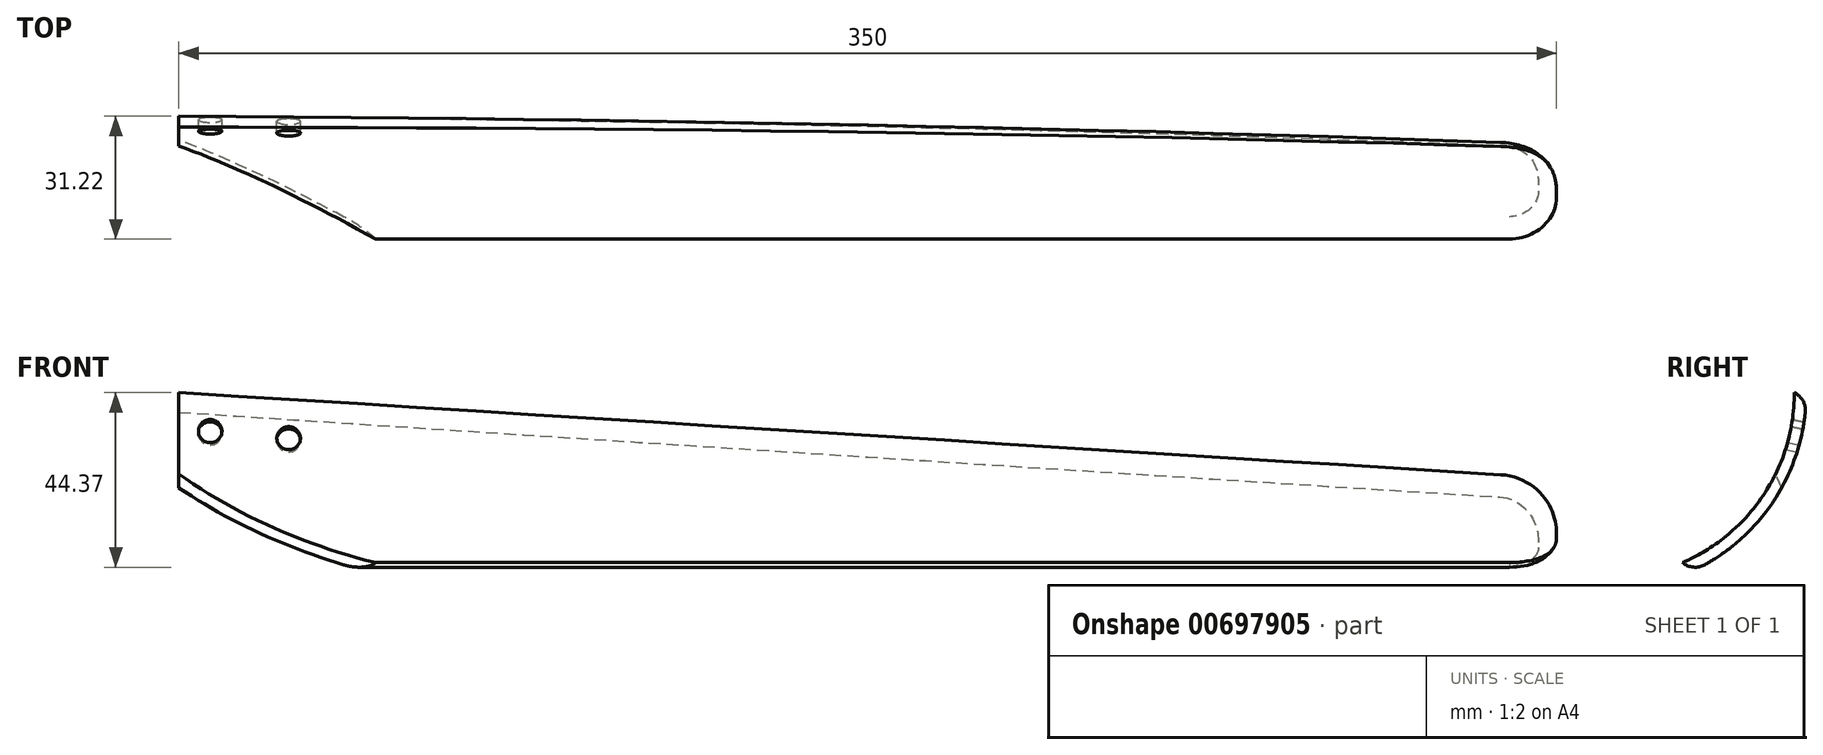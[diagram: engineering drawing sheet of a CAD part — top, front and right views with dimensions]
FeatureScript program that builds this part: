
annotation { "Feature Type Name" : "Feature", "Feature Type Description" : "" }
export const myFeature = defineFeature(function(context is Context, id is Id, definition is map)
    precondition{}
    {
        {
            assignVariable(context, id + "F0", {"name" : "longueur", "anyValue" : 350});
        }
        {
            var Q0;
            Q0=qCreatedBy(makeId("Right.planeOp"),FACE);
            var sketch = newSketch(context, id + "F1", { "sketchPlane" : qUnion([Q0])});
            skCircle(sketch, "E0", {"center": v(0, 0) * mm, "radius": 50 * mm});
            skCircle(sketch, "E1.0", {"center": v(0, 0) * mm, "radius": 47 * mm});
            skLineSegment(sketch, "E2", {"start": v(50, 0) * mm, "end": v(19.75, -45.93) * mm, "construction": true});
            skLineSegment(sketch, "E3", {"start": v(50, 0) * mm, "end": v(47, 0) * mm});
            skLineSegment(sketch, "E4", {"start": v(19.75, -45.93) * mm, "end": v(18.57, -43.18) * mm});
            skLineSegment(sketch, "E5", {"start": v(50, 0) * mm, "end": v(43.75, -24.2) * mm, "construction": true});
            skLineSegment(sketch, "E6", {"start": v(0, 0) * mm, "end": v(50, 0) * mm, "construction": true});
            skLineSegment(sketch, "E7.1.0", {"start": v(0, 0) * mm, "end": v(49.06, -9.65) * mm, "construction": true});
            skLineSegment(sketch, "E7.2.0", {"start": v(0, 0) * mm, "end": v(46.28, -18.93) * mm, "construction": true});
            skLineSegment(sketch, "E7.anchor2", {"start": v(0, 0) * mm, "end": v(19.75, -45.93) * mm, "construction": true});
            skLineSegment(sketch, "E8.2.3.0", {"start": v(0, 0) * mm, "end": v(41.76, -27.5) * mm, "construction": true});
            skLineSegment(sketch, "E8.2.4.0", {"start": v(0, 0) * mm, "end": v(35.67, -35.04) * mm, "construction": true});
            skLineSegment(sketch, "E9.2.5.0", {"start": v(0, 0) * mm, "end": v(28.24, -41.26) * mm, "construction": true});
            skSolve(sketch);
        }
        {
            var Q0;
            {var subQ0=sQuery(id+"F1.wireOp",EDGE,"E3");Q0=makeQuery(id+"F1.imprint","IMPRINT",FACE,{"disambiguationData":[TD([[makeQuery(id+"F1.imprint","IMPRINT",EDGE,{"derivedFrom":subQ0}),1.0]])]});}
            extrude(context, id + "F2", {"entities" : qUnion([Q0]), "depth" : (getVariable(context, 'longueur')) * mm, "offsetDistance" : 25 * mm});
        }
        {
            var Q0;
            Q0=makeQuery(id+"F2.opExtrude","CAP_FACE",FACE,{"disambiguationData":[OSD([sQuery(id+"F1.wireOp",EDGE,"E0"),sQuery(id+"F1.wireOp",EDGE,"E1.0"),sQuery(id+"F1.wireOp",EDGE,"E3"),sQuery(id+"F1.wireOp",EDGE,"E4")])],"isStart":false});
            var sketch = newSketch(context, id + "F3", { "sketchPlane" : qUnion([Q0])});
            skLineSegment(sketch, "E10", {"start": v(19.75, -45.93) * mm, "end": v(45.03, -21.73) * mm});
            skSolve(sketch);
        }
        {
            var Q0;
            Q0=makeQuery(id+"F2.opExtrude","CAP_VERTEX",VERTEX,{"disambiguationData":[OSD([sQuery(id+"F1.wireOp",EDGE,"E1.0"),sQuery(id+"F1.wireOp",EDGE,"E3")])],"isStart":true});
            var Q1;
            Q1=makeQuery(id+"F2.opExtrude","CAP_VERTEX",VERTEX,{"disambiguationData":[OSD([sQuery(id+"F1.wireOp",EDGE,"E0"),sQuery(id+"F1.wireOp",EDGE,"E3")])],"isStart":true});
            var Q2;
            Q2=sQuery(id+"F3.wireOp",VERTEX,"E10.end");
            cPlane(context, id + "F4", {"entities" : qUnion([Q0, Q1, Q2]), "cplaneType" : CPlaneType.THREE_POINT, "offset" : 25 * mm, "width" : 150 * mm, "height" : 150 * mm});
        }
        {
            var Q0;
            Q0=qCreatedBy(id+"F4.planeOp",FACE);
            var sketch = newSketch(context, id + "F5", { "sketchPlane" : qUnion([Q0])});
            skLineSegment(sketch, "E11.0", {"start": v(0, 50) * mm, "end": v(0, 47) * mm});
            skLineSegment(sketch, "E12", {"start": v(0, 50) * mm, "end": v(356.03, 68.4) * mm});
            skLineSegment(sketch, "E13", {"start": v(356.03, 68.4) * mm, "end": v(352, 18.56) * mm});
            skLineSegment(sketch, "E14", {"start": v(352, 18.57) * mm, "end": v(0, 47) * mm});
            skSolve(sketch);
        }
        {
            var Q0;
            Q0=qSketchRegion(id+"F5",true);
            extrude(context, id + "F6", {"entities" : qUnion([Q0]), "operationType" : NewBodyOperationType.REMOVE, "endBound" : BoundingType.THROUGH_ALL, "depth" : 25 * mm, "offsetDistance" : 25 * mm});
        }
        {
            var Q0;
            Q0=makeQuery(id+"F2.opExtrude","SWEPT_FACE",FACE,{"disambiguationData":[OSD([sQuery(id+"F1.wireOp",EDGE,"E4")])]});
            var sketch = newSketch(context, id + "F7", { "sketchPlane" : qUnion([Q0])});
            skLineSegment(sketch, "E15", {"start": v(0, -50) * mm, "end": v(50, -50) * mm});
            skLineSegment(sketch, "E16", {"start": v(50, -50) * mm, "end": v(50, -47) * mm});
            skSolve(sketch);
        }
        {
            var Q0;
            Q0=sQuery(id+"F7.wireOp",VERTEX,"E15.end");
            var Q1;
            Q1=sQuery(id+"F7.wireOp",VERTEX,"E16.end");
            var Q2;
            Q2=sQuery(id+"F1.wireOp",VERTEX,"E5.end");
            cPlane(context, id + "F8", {"entities" : qUnion([Q0, Q1, Q2]), "cplaneType" : CPlaneType.THREE_POINT, "offset" : 25 * mm, "width" : 150 * mm, "height" : 150 * mm});
        }
        {
            var Q0;
            Q0=qCreatedBy(id+"F8.planeOp",FACE);
            var sketch = newSketch(context, id + "F9", { "sketchPlane" : qUnion([Q0])});
            skLineSegment(sketch, "E17.bottom", {"start": v(26.95, -18.07) * mm, "end": v(-72.05, -18.07) * mm});
            skLineSegment(sketch, "E17.top", {"start": v(26.95, -70.26) * mm, "end": v(-72.05, -70.26) * mm});
            skLineSegment(sketch, "E17.left", {"start": v(26.95, -18.07) * mm, "end": v(26.95, -70.26) * mm});
            skLineSegment(sketch, "E17.right", {"start": v(-72.05, -18.07) * mm, "end": v(-72.05, -70.26) * mm});
            skSolve(sketch);
        }
        {
            var Q0;
            Q0=qSketchRegion(id+"F9",true);
            extrude(context, id + "F10", {"entities" : qUnion([Q0]), "operationType" : NewBodyOperationType.REMOVE, "endBound" : BoundingType.THROUGH_ALL, "oppositeDirection" : true, "depth" : 25 * mm, "offsetDistance" : 25 * mm});
        }
        {
            var Q0;
            Q0=makeQuery(id+"F6.boolean.opBoolean","INTERSECT",EDGE,{"derivedFrom":[makeQuery(id+"F2.opExtrude","CAP_FACE",FACE,{"disambiguationData":[OSD([sQuery(id+"F1.wireOp",EDGE,"E0"),sQuery(id+"F1.wireOp",EDGE,"E1.0"),sQuery(id+"F1.wireOp",EDGE,"E3"),sQuery(id+"F1.wireOp",EDGE,"E4")])],"isStart":false}),makeQuery(id+"F6.opExtrude","CAP_FACE",FACE,{"disambiguationData":[OSD([sQuery(id+"F5.wireOp",EDGE,"E11.0"),sQuery(id+"F5.wireOp",EDGE,"E12"),sQuery(id+"F5.wireOp",EDGE,"E13"),sQuery(id+"F5.wireOp",EDGE,"E14")])],"isStart":true})]});
            fillet(context, id + "F11", {"entities" : qUnion([Q0]), "radius" : 15 * mm, "tangentPropagation" : true, "allowEdgeOverflow" : false});
        }
        {
            var Q0;
            Q0=makeQuery(id+"F2.opExtrude","CAP_EDGE",EDGE,{"disambiguationData":[OSD([sQuery(id+"F1.wireOp",EDGE,"E4")])],"isStart":false});
            fillet(context, id + "F12", {"entities" : qUnion([Q0]), "radius" : 12 * mm, "tangentPropagation" : true, "allowEdgeOverflow" : false});
        }
        {
            var Q0;
            Q0=makeQuery(id+"F6.boolean.opBoolean","INTERSECT",EDGE,{"derivedFrom":[makeQuery(id+"F2.opExtrude","SWEPT_FACE",FACE,{"disambiguationData":[OSD([sQuery(id+"F1.wireOp",EDGE,"E0")])]}),makeQuery(id+"F6.opExtrude","CAP_FACE",FACE,{"disambiguationData":[OSD([sQuery(id+"F5.wireOp",EDGE,"E11.0"),sQuery(id+"F5.wireOp",EDGE,"E12"),sQuery(id+"F5.wireOp",EDGE,"E13"),sQuery(id+"F5.wireOp",EDGE,"E14")])],"isStart":true})]});
            fillet(context, id + "F13", {"entities" : qUnion([Q0]), "radius" : 5 * mm, "tangentPropagation" : true, "allowEdgeOverflow" : false});
        }
        {
            var Q0;
            Q0=sQuery(id+"F1.wireOp",VERTEX,"E7.1.0.end");
            var Q1;
            Q1=sQuery(id+"F1.wireOp",EDGE,"E7.1.0");
            cPlane(context, id + "F14", {"entities" : qUnion([Q0, Q1]), "cplaneType" : CPlaneType.LINE_POINT, "offset" : 25 * mm, "width" : 150 * mm, "height" : 150 * mm});
        }
        {
            var Q0;
            Q0=qCreatedBy(id+"F14.planeOp",FACE);
            var sketch = newSketch(context, id + "F15", { "sketchPlane" : qUnion([Q0])});
            skLineSegment(sketch, "E18", {"start": v(-7.97, -0.74) * mm, "end": v(-27.88, -2.58) * mm, "construction": true});
            skCircle(sketch, "E19", {"center": v(-7.97, -0.74) * mm, "radius": 3 * mm});
            skCircle(sketch, "E20", {"center": v(-27.88, -2.58) * mm, "radius": 3 * mm});
            skSolve(sketch);
        }
        {
            var Q0;
            Q0=qSketchRegion(id+"F15",true);
            extrude(context, id + "F16", {"entities" : qUnion([Q0]), "operationType" : NewBodyOperationType.REMOVE, "endBound" : BoundingType.THROUGH_ALL, "oppositeDirection" : true, "depth" : 25 * mm, "offsetDistance" : 25 * mm});
        }
    });
